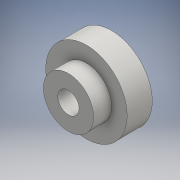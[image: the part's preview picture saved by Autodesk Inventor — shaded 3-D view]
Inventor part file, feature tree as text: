
AUTODESK INVENTOR PART (.ipt)
format: ipt  version: 2016 (Build 200138000, 138)  size: 118,272 bytes
history: native  units: mm
features: sketch x3, extrude x2, hole x1
ambient origin geometry x8: Origin, YZ Plane, XZ Plane, XY Plane, X Axis, Y Axis, Z Axis, Center Point
bodies: Solid1 (feature_tree)
feature tree (6):
  extrude  "Extrusion1"  Depth=7.9mm TaperAngle=0.0deg
  extrude  "Extrusion2"  Depth=3.3mm TaperAngle=0.0deg
  hole  "Hole1"  [1 undecoded]
  sketch  "Sketch1"  dims[d0=14.9mm d1=7.9mm d2=0.0mm]
  sketch  "Sketch2"  dims[d3=9.2mm d4=3.3mm d5=0.0mm]
  sketch  "Sketch3"  dims[d6=3.9mm d7=6.0mm d8=4.0mm d9=2.0mm d10=90.0deg d11=8.0mm d12=20.594885mm]
note: 1 required parameter value undecoded (feature->parameter linkage not recoverable at this tier; creation-order binding heuristic only, values carry confidence <= 0.55)
